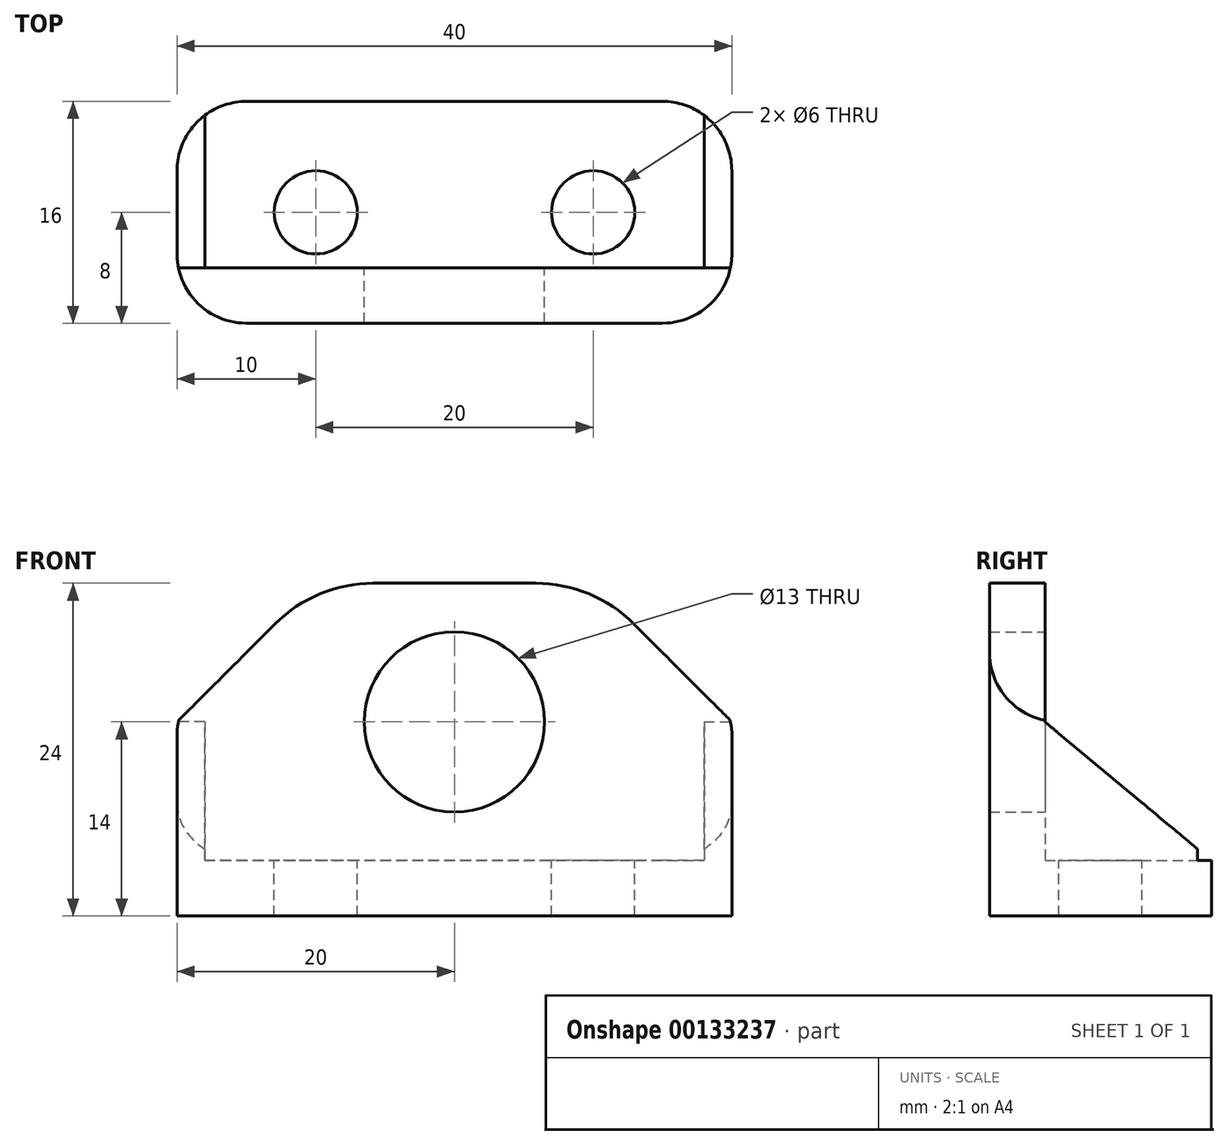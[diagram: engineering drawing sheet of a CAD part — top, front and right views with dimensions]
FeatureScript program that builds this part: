
annotation { "Feature Type Name" : "Feature", "Feature Type Description" : "" }
export const myFeature = defineFeature(function(context is Context, id is Id, definition is map)
    precondition{}
    {
        {
            var Q0;
            Q0=qCreatedBy(makeId("Top.planeOp"),FACE);
            var sketch = newSketch(context, id + "F0", { "sketchPlane" : qUnion([Q0])});
            skLineSegment(sketch, "E0.bottom", {"start": v(20, -8) * mm, "end": v(-20, -8) * mm});
            skLineSegment(sketch, "E0.top", {"start": v(20, 8) * mm, "end": v(-20, 8) * mm});
            skLineSegment(sketch, "E0.left", {"start": v(20, -8) * mm, "end": v(20, 8) * mm});
            skLineSegment(sketch, "E0.right", {"start": v(-20, -8) * mm, "end": v(-20, 8) * mm});
            skPoint(sketch, "E0.middle", {"position": v(0, 0) * mm});
            skSolve(sketch);
        }
        {
            var Q0;
            Q0=makeQuery(id+"F0.imprint","IMPRINT",FACE,{"disambiguationData":[TD([[makeQuery(id+"F0.imprint","IMPRINT",EDGE,{"derivedFrom":sQuery(id+"F0.wireOp",EDGE,"E0.bottom")}),-1.0]])]});
            extrude(context, id + "F1", {"entities" : qUnion([Q0]), "depth" : 4 * mm});
        }
        {
            var Q0;
            Q0=makeQuery(id+"F1.opExtrude","CAP_FACE",FACE,{"disambiguationData":[OSD([sQuery(id+"F0.wireOp",EDGE,"E0.bottom"),sQuery(id+"F0.wireOp",EDGE,"E0.top"),sQuery(id+"F0.wireOp",EDGE,"E0.left"),sQuery(id+"F0.wireOp",EDGE,"E0.right")])],"isStart":false});
            var sketch = newSketch(context, id + "F2", { "sketchPlane" : qUnion([Q0])});
            skPoint(sketch, "E1", {"position": v(10, 0) * mm});
            skPoint(sketch, "E2", {"position": v(-10, 0) * mm});
            skLineSegment(sketch, "E3.bottom", {"start": v(-20, -8) * mm, "end": v(20, -8) * mm});
            skLineSegment(sketch, "E3.top", {"start": v(-20, -4) * mm, "end": v(20, -4) * mm});
            skLineSegment(sketch, "E3.left", {"start": v(-20, -8) * mm, "end": v(-20, -4) * mm});
            skLineSegment(sketch, "E3.right", {"start": v(20, -8) * mm, "end": v(20, -4) * mm});
            skSolve(sketch);
        }
        {
            var Q0;
            Q0=makeQuery(id+"F2.imprint","IMPRINT",FACE,{"disambiguationData":[TD([[makeQuery(id+"F2.imprint","IMPRINT",EDGE,{"derivedFrom":sQuery(id+"F2.wireOp",EDGE,"E3.bottom")}),-1.0]])]});
            extrude(context, id + "F3", {"entities" : qUnion([Q0]), "operationType" : NewBodyOperationType.ADD, "depth" : 20 * mm});
        }
        {
            var Q0;
            Q0=sQuery(id+"F2.wireOp",VERTEX,"E2");
            var Q1;
            Q1=sQuery(id+"F2.wireOp",VERTEX,"E1");
            var Q2;
            Q2=makeQuery(id+"F1.opExtrude","SWEPT_BODY",BODY,{"disambiguationData":[OSD([sQuery(id+"F0.wireOp",EDGE,"E0.bottom"),sQuery(id+"F0.wireOp",EDGE,"E0.top"),sQuery(id+"F0.wireOp",EDGE,"E0.left"),sQuery(id+"F0.wireOp",EDGE,"E0.right")])]});
            hole(context, id + "F4", {"style" : HoleStyle.SIMPLE, "endStyle" : HoleEndStyle.THROUGH, "holeDiameter" : 6 * mm, "locations" : qUnion([Q0, Q1]), "scope" : qUnion([Q2]), "isTappedThrough" : true});
        }
        {
            var Q0;
            Q0=makeQuery(id+"F3.opExtrude","SWEPT_FACE",FACE,{"disambiguationData":[OSD([sQuery(id+"F2.wireOp",EDGE,"E3.top")])]});
            var sketch = newSketch(context, id + "F5", { "sketchPlane" : qUnion([Q0])});
            skPoint(sketch, "E4", {"position": v(0, 14) * mm});
            skSolve(sketch);
        }
        {
            var Q0;
            Q0=sQuery(id+"F5.wireOp",VERTEX,"E4");
            var Q1;
            Q1=makeQuery(id+"F1.opExtrude","SWEPT_BODY",BODY,{"disambiguationData":[OSD([sQuery(id+"F0.wireOp",EDGE,"E0.bottom"),sQuery(id+"F0.wireOp",EDGE,"E0.top"),sQuery(id+"F0.wireOp",EDGE,"E0.left"),sQuery(id+"F0.wireOp",EDGE,"E0.right")])]});
            hole(context, id + "F12", {"style" : HoleStyle.SIMPLE, "endStyle" : HoleEndStyle.THROUGH, "holeDiameter" : 13 * mm, "locations" : qUnion([Q0]), "scope" : qUnion([Q1]), "isTappedThrough" : true});
        }
        {
            var Q0;
            Q0=makeQuery(id+"F3.opExtrude","CAP_EDGE",EDGE,{"disambiguationData":[OSD([sQuery(id+"F2.wireOp",EDGE,"E3.left")])],"isStart":false});
            var Q1;
            Q1=makeQuery(id+"F3.opExtrude","CAP_EDGE",EDGE,{"disambiguationData":[OSD([sQuery(id+"F2.wireOp",EDGE,"E3.right")])],"isStart":false});
            chamfer(context, id + "F6", {"entities" : qUnion([Q0, Q1]), "width" : 10 * mm, "tangentPropagation" : true});
        }
        {
            var Q0;
            Q0=makeQuery(id+"F3.boolean.opBoolean","MERGE",FACE,{"derivedFrom":[makeQuery(id+"F1.opExtrude","SWEPT_FACE",FACE,{"disambiguationData":[OSD([sQuery(id+"F0.wireOp",EDGE,"E0.right")])]}),makeQuery(id+"F3.opExtrude","SWEPT_FACE",FACE,{"disambiguationData":[OSD([sQuery(id+"F2.wireOp",EDGE,"E3.left")])]})]});
            var sketch = newSketch(context, id + "F7", { "sketchPlane" : qUnion([Q0])});
            skLineSegment(sketch, "E5", {"start": v(-8, 4) * mm, "end": v(4, 14) * mm});
            skSolve(sketch);
        }
        {
            var Q0;
            Q0=makeQuery(id+"F7.imprint","IMPRINT",FACE,{"disambiguationData":[TD([[makeQuery(id+"F7.imprint","IMPRINT",EDGE,{"derivedFrom":sQuery(id+"F7.wireOp",EDGE,"E5")}),-1.0]])]});
            extrude(context, id + "F8", {"entities" : qUnion([Q0]), "operationType" : NewBodyOperationType.ADD, "oppositeDirection" : true, "depth" : 2 * mm});
        }
        {
            var Q0;
            Q0=makeQuery(id+"F3.boolean.opBoolean","MERGE",FACE,{"derivedFrom":[makeQuery(id+"F1.opExtrude","SWEPT_FACE",FACE,{"disambiguationData":[OSD([sQuery(id+"F0.wireOp",EDGE,"E0.left")])]}),makeQuery(id+"F3.opExtrude","SWEPT_FACE",FACE,{"disambiguationData":[OSD([sQuery(id+"F2.wireOp",EDGE,"E3.right")])]})]});
            var sketch = newSketch(context, id + "F13", { "sketchPlane" : qUnion([Q0])});
            skLineSegment(sketch, "E6", {"start": v(8, 4) * mm, "end": v(-4, 14) * mm});
            skSolve(sketch);
        }
        {
            var Q0;
            Q0=makeQuery(id+"F13.imprint","IMPRINT",FACE,{"disambiguationData":[TD([[makeQuery(id+"F13.imprint","IMPRINT",EDGE,{"derivedFrom":sQuery(id+"F13.wireOp",EDGE,"E6")}),1.0]])]});
            extrude(context, id + "F9", {"entities" : qUnion([Q0]), "operationType" : NewBodyOperationType.ADD, "oppositeDirection" : true, "depth" : 2 * mm});
        }
        {
            var Q0;
            Q0=makeQuery(id+"F1.opExtrude","SWEPT_EDGE",EDGE,{"disambiguationData":[OSD([sQuery(id+"F0.wireOp",EDGE,"E0.top"),sQuery(id+"F0.wireOp",EDGE,"E0.left")])]});
            var Q1;
            Q1=makeQuery(id+"F1.opExtrude","SWEPT_EDGE",EDGE,{"disambiguationData":[OSD([sQuery(id+"F0.wireOp",EDGE,"E0.top"),sQuery(id+"F0.wireOp",EDGE,"E0.right")])]});
            var Q2;
            Q2=makeQuery(id+"F3.boolean.opBoolean","MERGE",EDGE,{"derivedFrom":[makeQuery(id+"F1.opExtrude","SWEPT_EDGE",EDGE,{"disambiguationData":[OSD([sQuery(id+"F0.wireOp",EDGE,"E0.bottom"),sQuery(id+"F0.wireOp",EDGE,"E0.right")])]}),makeQuery(id+"F3.opExtrude","SWEPT_EDGE",EDGE,{"disambiguationData":[OSD([sQuery(id+"F2.wireOp",EDGE,"E3.bottom"),sQuery(id+"F2.wireOp",EDGE,"E3.left")])]})]});
            var Q3;
            Q3=makeQuery(id+"F3.boolean.opBoolean","MERGE",EDGE,{"derivedFrom":[makeQuery(id+"F1.opExtrude","SWEPT_EDGE",EDGE,{"disambiguationData":[OSD([sQuery(id+"F0.wireOp",EDGE,"E0.bottom"),sQuery(id+"F0.wireOp",EDGE,"E0.left")])]}),makeQuery(id+"F3.opExtrude","SWEPT_EDGE",EDGE,{"disambiguationData":[OSD([sQuery(id+"F2.wireOp",EDGE,"E3.bottom"),sQuery(id+"F2.wireOp",EDGE,"E3.right")])]})]});
            fillet(context, id + "F10", {"entities" : qUnion([Q0, Q1, Q2, Q3]), "radius" : 5 * mm, "tangentPropagation" : true, "allowEdgeOverflow" : false});
        }
        {
            var Q0;
            {var subQ0=sQuery(id+"F2.wireOp",EDGE,"E3.right");Q0=makeQuery(id+"F6.opChamfer","BLEND_EDGE",EDGE,{"blendedFrom":[makeQuery(id+"F3.opExtrude","CAP_EDGE",EDGE,{"disambiguationData":[OSD([subQ0])],"isStart":false}),makeQuery(id+"F3.opExtrude","CAP_FACE",FACE,{"disambiguationData":[OSD([sQuery(id+"F2.wireOp",EDGE,"E3.bottom"),sQuery(id+"F2.wireOp",EDGE,"E3.top"),sQuery(id+"F2.wireOp",EDGE,"E3.left"),subQ0])],"isStart":false})],"blendedInto":[makeQuery(id+"F3.opExtrude","CAP_FACE",FACE,{"disambiguationData":[OSD([sQuery(id+"F2.wireOp",EDGE,"E3.bottom"),sQuery(id+"F2.wireOp",EDGE,"E3.top"),sQuery(id+"F2.wireOp",EDGE,"E3.left"),subQ0])],"isStart":false})]});}
            var Q1;
            {var subQ0=sQuery(id+"F2.wireOp",EDGE,"E3.left");Q1=makeQuery(id+"F6.opChamfer","BLEND_EDGE",EDGE,{"blendedFrom":[makeQuery(id+"F3.opExtrude","CAP_EDGE",EDGE,{"disambiguationData":[OSD([subQ0])],"isStart":false}),makeQuery(id+"F3.opExtrude","CAP_FACE",FACE,{"disambiguationData":[OSD([sQuery(id+"F2.wireOp",EDGE,"E3.bottom"),sQuery(id+"F2.wireOp",EDGE,"E3.top"),subQ0,sQuery(id+"F2.wireOp",EDGE,"E3.right")])],"isStart":false})],"blendedInto":[makeQuery(id+"F3.opExtrude","CAP_FACE",FACE,{"disambiguationData":[OSD([sQuery(id+"F2.wireOp",EDGE,"E3.bottom"),sQuery(id+"F2.wireOp",EDGE,"E3.top"),subQ0,sQuery(id+"F2.wireOp",EDGE,"E3.right")])],"isStart":false})]});}
            fillet(context, id + "F11", {"entities" : qUnion([Q0, Q1]), "radius" : 10 * mm, "tangentPropagation" : true, "allowEdgeOverflow" : false});
        }
    });
